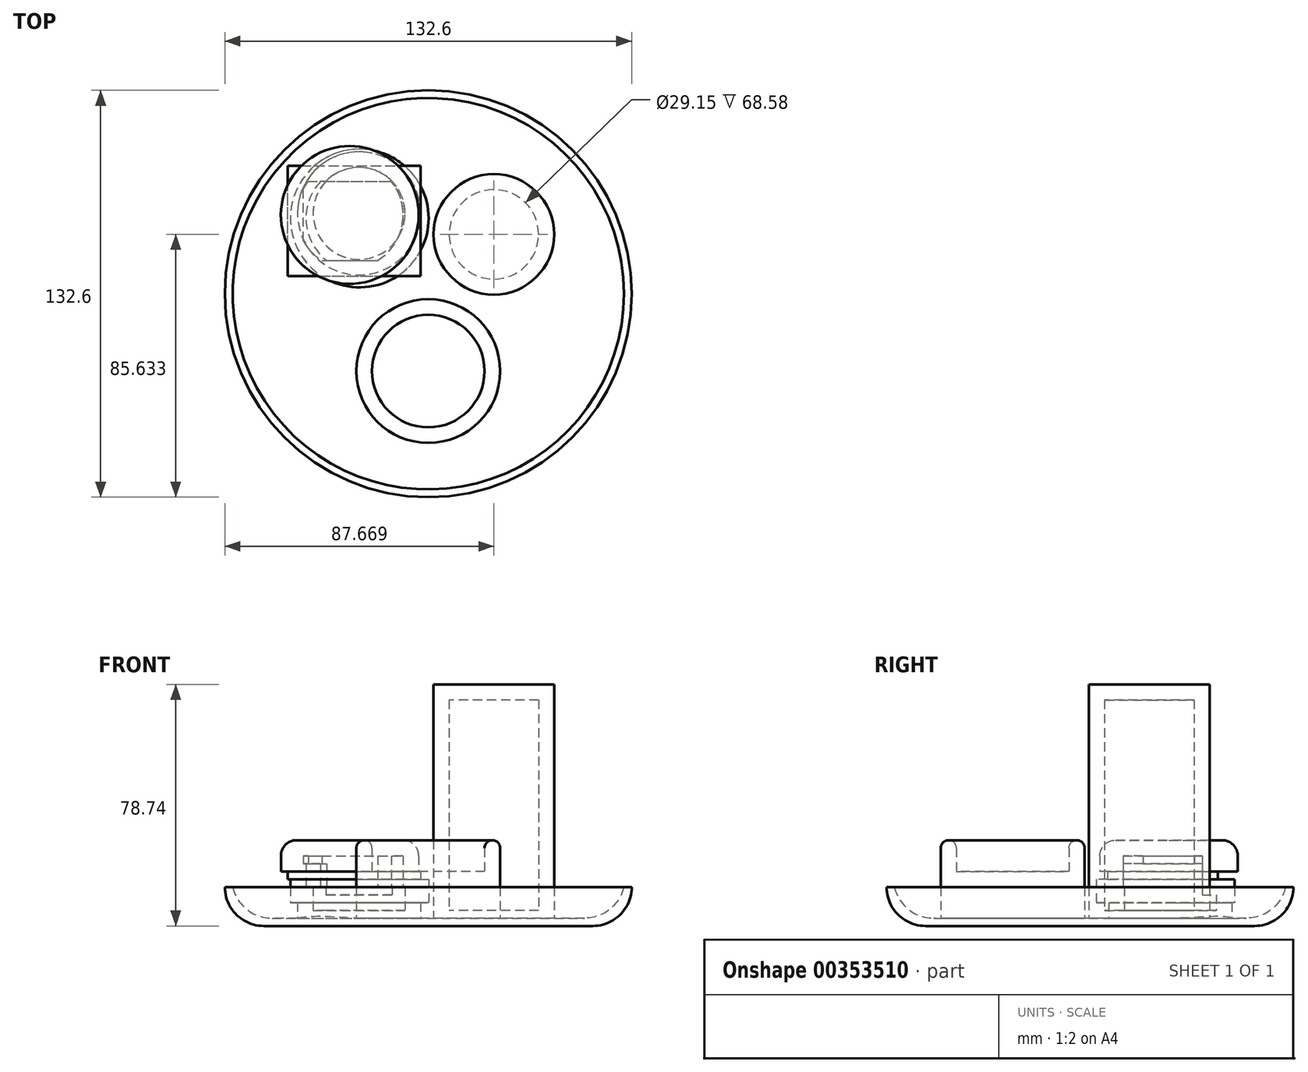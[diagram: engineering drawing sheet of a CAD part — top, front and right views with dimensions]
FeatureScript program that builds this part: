
annotation { "Feature Type Name" : "Feature", "Feature Type Description" : "" }
export const myFeature = defineFeature(function(context is Context, id is Id, definition is map)
    precondition{}
    {
        {
            var Q0;
            Q0=qCreatedBy(makeId("Top.planeOp"),FACE);
            var sketch = newSketch(context, id + "F0", { "sketchPlane" : qUnion([Q0])});
            skCircle(sketch, "E0", {"center": v(0, 0) * mm, "radius": 66.3 * mm});
            skSolve(sketch);
        }
        {
            var Q0;
            Q0=makeQuery(id+"F0.imprint","IMPRINT",FACE,{"disambiguationData":[TD([[makeQuery(id+"F0.imprint","IMPRINT",EDGE,{"derivedFrom":sQuery(id+"F0.wireOp",EDGE,"E0")}),1.0]])]});
            extrude(context, id + "F1", {"entities" : qUnion([Q0]), "depth" : 12.7 * mm});
        }
        {
            var Q0;
            Q0=makeQuery(id+"F1.opExtrude","CAP_FACE",FACE,{"disambiguationData":[OSD([sQuery(id+"F0.wireOp",EDGE,"E0")])],"isStart":false});
            shell(context, id + "F2", {"entities" : qUnion([Q0]), "thickness" : 2.54 * mm});
        }
        {
            var Q0;
            {var subQ0=sQuery(id+"F0.wireOp",EDGE,"E0");Q0=makeQuery(id+"F2.opShell","OFFSET_EDGE",EDGE,{"disambiguationData":[OSD([subQ0]),TDD([makeQuery(id+"F1.opExtrude","CAP_EDGE",EDGE,{"disambiguationData":[OSD([subQ0])],"isStart":true})])]});}
            fillet(context, id + "F3", {"entities" : qUnion([Q0]), "radius" : 13.2 * mm, "tangentPropagation" : true, "allowEdgeOverflow" : false});
        }
        {
            var Q0;
            {var subQ0=sQuery(id+"F0.wireOp",EDGE,"E0");Q0=makeQuery(id+"F2.opShell","OFFSET_FACE",FACE,{"disambiguationData":[OSD([subQ0]),TDD([makeQuery(id+"F1.opExtrude","CAP_FACE",FACE,{"disambiguationData":[OSD([subQ0])],"isStart":true})])]});}
            var sketch = newSketch(context, id + "F4", { "sketchPlane" : qUnion([Q0])});
            skCircle(sketch, "E1", {"center": v(-22.56, 26.17) * mm, "radius": 20.07 * mm});
            skSolve(sketch);
        }
        {
            var Q0;
            Q0 = qSketchRegion(id + "F4", true);
            extrude(context, id + "F5", {"entities" : qUnion([Q0]), "operationType" : NewBodyOperationType.ADD, "depth" : 5.08 * mm});
        }
        {
            var Q0;
            Q0=makeQuery(id+"F5.opExtrude","CAP_FACE",FACE,{"disambiguationData":[OSD([sQuery(id+"F4.wireOp",EDGE,"E1")])],"isStart":false});
            var sketch = newSketch(context, id + "F6", { "sketchPlane" : qUnion([Q0])});
            skSolve(sketch);
        }
        {
            var Q0;
            Q0=makeQuery(id+"F1.opExtrude","CAP_EDGE",EDGE,{"disambiguationData":[OSD([sQuery(id+"F0.wireOp",EDGE,"E0")])],"isStart":true});
            fillet(context, id + "F7", {"entities" : qUnion([Q0]), "radius" : 12.7 * mm, "tangentPropagation" : true, "allowEdgeOverflow" : false});
        }
        {
            var Q0;
            Q0=makeQuery(id+"F6.imprint","IMPRINT",FACE,{"disambiguationData":[TD([[makeQuery(id+"F6.imprint","IMPRINT",EDGE,{"derivedFrom":makeQuery(id+"F5.opExtrude","CAP_EDGE",EDGE,{"disambiguationData":[OSD([sQuery(id+"F4.wireOp",EDGE,"E1")])],"isStart":false})}),1.0]])]});
            var sketch = newSketch(context, id + "F8", { "sketchPlane" : qUnion([Q0])});
            skCircle(sketch, "E2", {"center": v(-22.4, 24.58) * mm, "radius": 22.53 * mm});
            skSolve(sketch);
        }
        {
            var Q0;
            Q0=makeQuery(id+"F8.imprint","IMPRINT",FACE,{"disambiguationData":[TD([[makeQuery(id+"F8.imprint","IMPRINT",EDGE,{"derivedFrom":sQuery(id+"F8.wireOp",EDGE,"E2")}),1.0]])]});
            var Q1;
            Q1=makeQuery(id+"F6.imprint","IMPRINT",FACE,{"disambiguationData":[TD([[makeQuery(id+"F6.imprint","IMPRINT",EDGE,{"derivedFrom":makeQuery(id+"F5.opExtrude","CAP_EDGE",EDGE,{"disambiguationData":[OSD([sQuery(id+"F4.wireOp",EDGE,"E1")])],"isStart":false})}),1.0]])]});
            extrude(context, id + "F9", {"entities" : qUnion([Q0, Q1]), "operationType" : NewBodyOperationType.ADD, "depth" : 7.62 * mm});
        }
        {
            var Q0;
            {var subQ0=sQuery(id+"F4.wireOp",EDGE,"E1");Q0=makeQuery(id+"F9.boolean.opBoolean","MERGE",FACE,{"derivedFrom":[makeQuery(id+"F9.opExtrude","CAP_FACE",FACE,{"disambiguationData":[OSD([subQ0])],"isStart":false}),makeQuery(id+"F9.opExtrude","CAP_FACE",FACE,{"disambiguationData":[OSD([subQ0,sQuery(id+"F8.wireOp",EDGE,"E2")])],"isStart":false})]});}
            var sketch = newSketch(context, id + "F10", { "sketchPlane" : qUnion([Q0])});
            skLineSegment(sketch, "E3.bottom", {"start": v(-45.85, 5.78) * mm, "end": v(-2.45, 5.78) * mm});
            skLineSegment(sketch, "E3.top", {"start": v(-45.85, 41.64) * mm, "end": v(-2.45, 41.64) * mm});
            skLineSegment(sketch, "E3.left", {"start": v(-45.85, 5.78) * mm, "end": v(-45.85, 41.64) * mm});
            skLineSegment(sketch, "E3.right", {"start": v(-2.45, 5.78) * mm, "end": v(-2.45, 41.64) * mm});
            skSolve(sketch);
        }
        {
            var Q0;
            Q0 = qSketchRegion(id + "F10", true);
            extrude(context, id + "F11", {"entities" : qUnion([Q0]), "operationType" : NewBodyOperationType.ADD, "depth" : 2.54 * mm});
        }
        {
            var Q0;
            Q0=makeQuery(id+"F11.opExtrude","CAP_FACE",FACE,{"disambiguationData":[OSD([sQuery(id+"F10.wireOp",EDGE,"E3.bottom"),sQuery(id+"F10.wireOp",EDGE,"E3.top"),sQuery(id+"F10.wireOp",EDGE,"E3.left"),sQuery(id+"F10.wireOp",EDGE,"E3.right")])],"isStart":false});
            var sketch = newSketch(context, id + "F12", { "sketchPlane" : qUnion([Q0])});
            skCircle(sketch, "E4", {"center": v(-25.57, 25.67) * mm, "radius": 22.46 * mm});
            skSolve(sketch);
        }
        {
            var Q0;
            Q0 = qSketchRegion(id + "F12", true);
            extrude(context, id + "F13", {"entities" : qUnion([Q0]), "operationType" : NewBodyOperationType.ADD, "depth" : 10.16 * mm});
        }
        {
            var Q0;
            Q0=makeQuery(id+"F13.opExtrude","CAP_EDGE",EDGE,{"disambiguationData":[OSD([sQuery(id+"F12.wireOp",EDGE,"E4")])],"isStart":false});
            fillet(context, id + "F14", {"entities" : qUnion([Q0]), "radius" : 5.08 * mm, "tangentPropagation" : true, "allowEdgeOverflow" : false});
        }
        {
            var Q0;
            {var subQ0=sQuery(id+"F0.wireOp",EDGE,"E0");Q0=makeQuery(id+"F2.opShell","OFFSET_FACE",FACE,{"disambiguationData":[OSD([subQ0]),TDD([makeQuery(id+"F1.opExtrude","CAP_FACE",FACE,{"disambiguationData":[OSD([subQ0])],"isStart":true})])]});}
            var sketch = newSketch(context, id + "F15", { "sketchPlane" : qUnion([Q0])});
            skCircle(sketch, "E5", {"center": v(21.37, 19.33) * mm, "radius": 19.65 * mm});
            skSolve(sketch);
        }
        {
            var Q0;
            Q0=sQuery(id+"F15.wireOp",EDGE,"E5");
            extrude(context, id + "F16", {"bodyType" : ToolBodyType.SURFACE, "surfaceEntities" : qUnion([Q0]), "depth" : 76.2 * mm});
        }
        {
            var Q0;
            Q0 = qSketchRegion(id + "F15", true);
            extrude(context, id + "F17", {"entities" : qUnion([Q0]), "operationType" : NewBodyOperationType.ADD, "depth" : 76.2 * mm});
        }
        {
            var Q0;
            Q0=makeQuery(id+"F17.opExtrude","CAP_FACE",FACE,{"disambiguationData":[OSD([sQuery(id+"F15.wireOp",EDGE,"E5")])],"isStart":false});
            var sketch = newSketch(context, id + "F18", { "sketchPlane" : qUnion([Q0])});
            skCircle(sketch, "E6", {"center": v(31.16, 21.64) * mm, "radius": 3.22 * mm});
            skSolve(sketch);
        }
        {
            var Q0;
            Q0=sQuery(id+"F18.wireOp",EDGE,"E6");
            extrude(context, id + "F19", {"bodyType" : ToolBodyType.SURFACE, "surfaceEntities" : qUnion([Q0]), "depth" : 50.8 * mm});
        }
        {
            var Q0;
            {var subQ0=sQuery(id+"F0.wireOp",EDGE,"E0");Q0=makeQuery(id+"F2.opShell","OFFSET_FACE",FACE,{"disambiguationData":[OSD([subQ0]),TDD([makeQuery(id+"F1.opExtrude","CAP_FACE",FACE,{"disambiguationData":[OSD([subQ0])],"isStart":true})])]});}
            var sketch = newSketch(context, id + "F20", { "sketchPlane" : qUnion([Q0])});
            skCircle(sketch, "E7", {"center": v(0, -25.2) * mm, "radius": 23.42 * mm});
            skSolve(sketch);
        }
        {
            var Q0;
            Q0=makeQuery(id+"F20.imprint","IMPRINT",FACE,{"disambiguationData":[TD([[makeQuery(id+"F20.imprint","IMPRINT",EDGE,{"derivedFrom":sQuery(id+"F20.wireOp",EDGE,"E7")}),1.0]])]});
            extrude(context, id + "F21", {"entities" : qUnion([Q0]), "operationType" : NewBodyOperationType.ADD, "depth" : 25.4 * mm});
        }
        {
            var Q0;
            Q0=makeQuery(id+"F21.opExtrude","CAP_FACE",FACE,{"disambiguationData":[OSD([sQuery(id+"F20.wireOp",EDGE,"E7")])],"isStart":false});
            shell(context, id + "F22", {"entities" : qUnion([Q0]), "thickness" : 5.08 * mm});
        }
        {
            var Q0;
            Q0=makeQuery(id+"F21.opExtrude","CAP_FACE",FACE,{"disambiguationData":[OSD([sQuery(id+"F20.wireOp",EDGE,"E7")])],"isStart":false});
            fillet(context, id + "F23", {"entities" : qUnion([Q0]), "radius" : 2.54 * mm, "tangentPropagation" : true, "allowEdgeOverflow" : false});
        }
        {
            var Q0;
            Q0=makeQuery(id+"F22.opShell","OFFSET_FACE",FACE,{"disambiguationData":[OSD([sQuery(id+"F0.wireOp",EDGE,"E0")]),OD(2.0)]});
            extrude(context, id + "F24", {"entities" : qUnion([Q0]), "operationType" : NewBodyOperationType.ADD, "depth" : 12.7 * mm});
        }
    });
